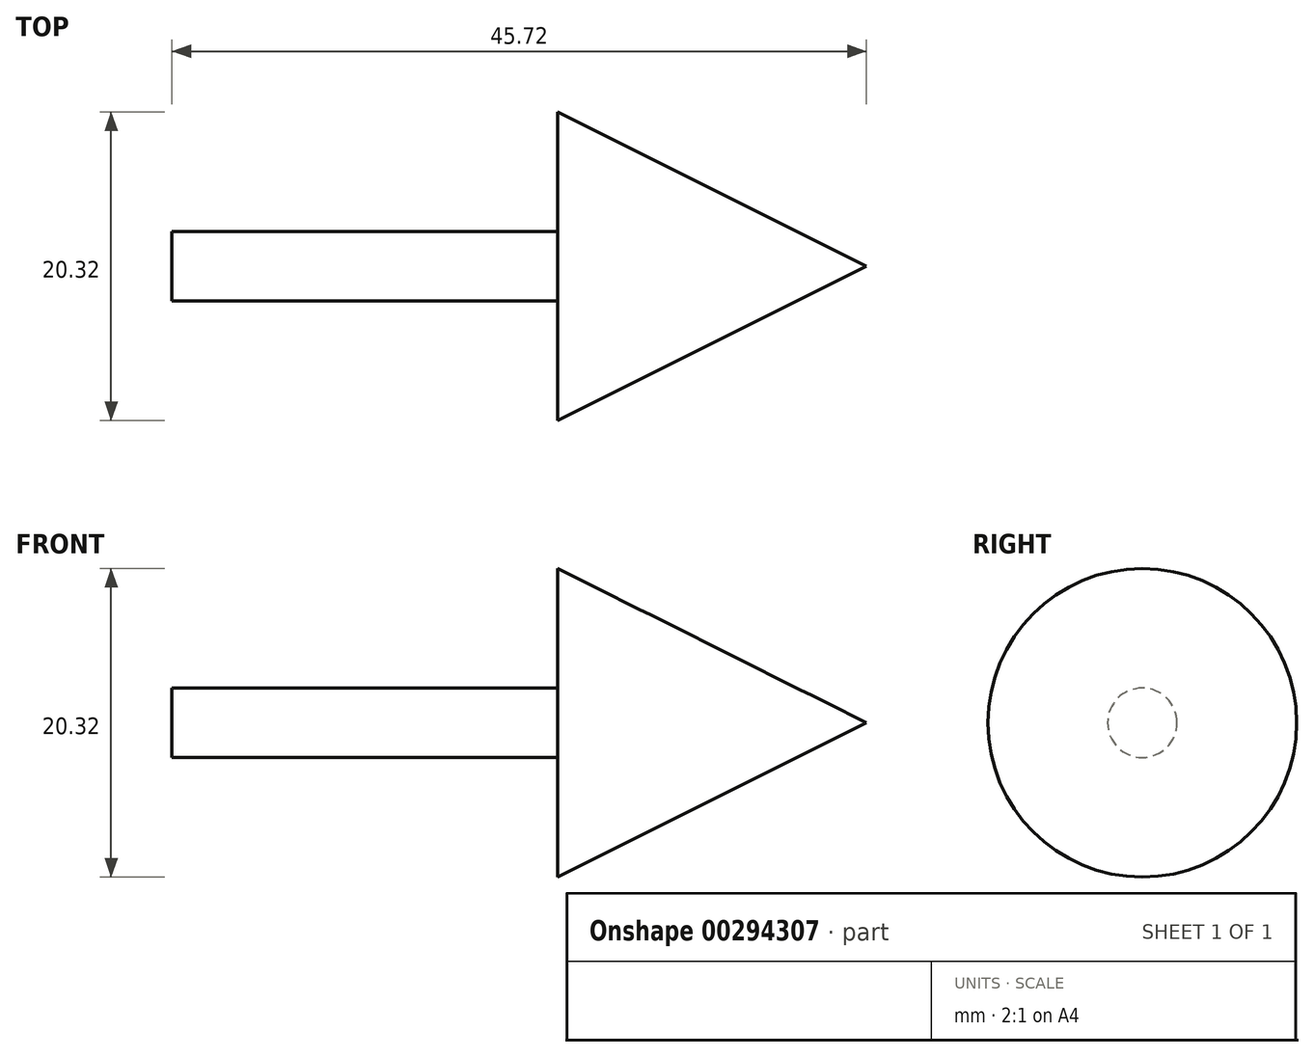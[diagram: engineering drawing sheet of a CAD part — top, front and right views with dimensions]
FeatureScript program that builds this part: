
annotation { "Feature Type Name" : "Feature", "Feature Type Description" : "" }
export const myFeature = defineFeature(function(context is Context, id is Id, definition is map)
    precondition{}
    {
        {
            var Q0;
            Q0=qCreatedBy(makeId("Front.planeOp"),FACE);
            var sketch = newSketch(context, id + "F0", { "sketchPlane" : qUnion([Q0])});
            skLineSegment(sketch, "E0", {"start": v(0, 0) * mm, "end": v(0, 2.29) * mm});
            skLineSegment(sketch, "E1", {"start": v(0, 2.29) * mm, "end": v(25.4, 2.29) * mm});
            skLineSegment(sketch, "E2", {"start": v(25.4, 2.29) * mm, "end": v(25.4, 10.16) * mm});
            skLineSegment(sketch, "E3", {"start": v(25.4, 10.16) * mm, "end": v(45.72, 0) * mm});
            skLineSegment(sketch, "E4", {"start": v(45.72, 0) * mm, "end": v(0, 0) * mm});
            skLineSegment(sketch, "E5", {"start": v(0, 0) * mm, "end": v(-3.3, 0) * mm, "construction": true});
            skSolve(sketch);
        }
        {
            var Q0;
            Q0 = qSketchRegion(id + "F0", true);
            var Q1;
            Q1=sQuery(id+"F0.wireOp",EDGE,"E5");
            revolve(context, id + "F1", {"entities" : qUnion([Q0]), "axis" : qUnion([Q1]), "revolveType" : RevolveType.FULL});
        }
    });
